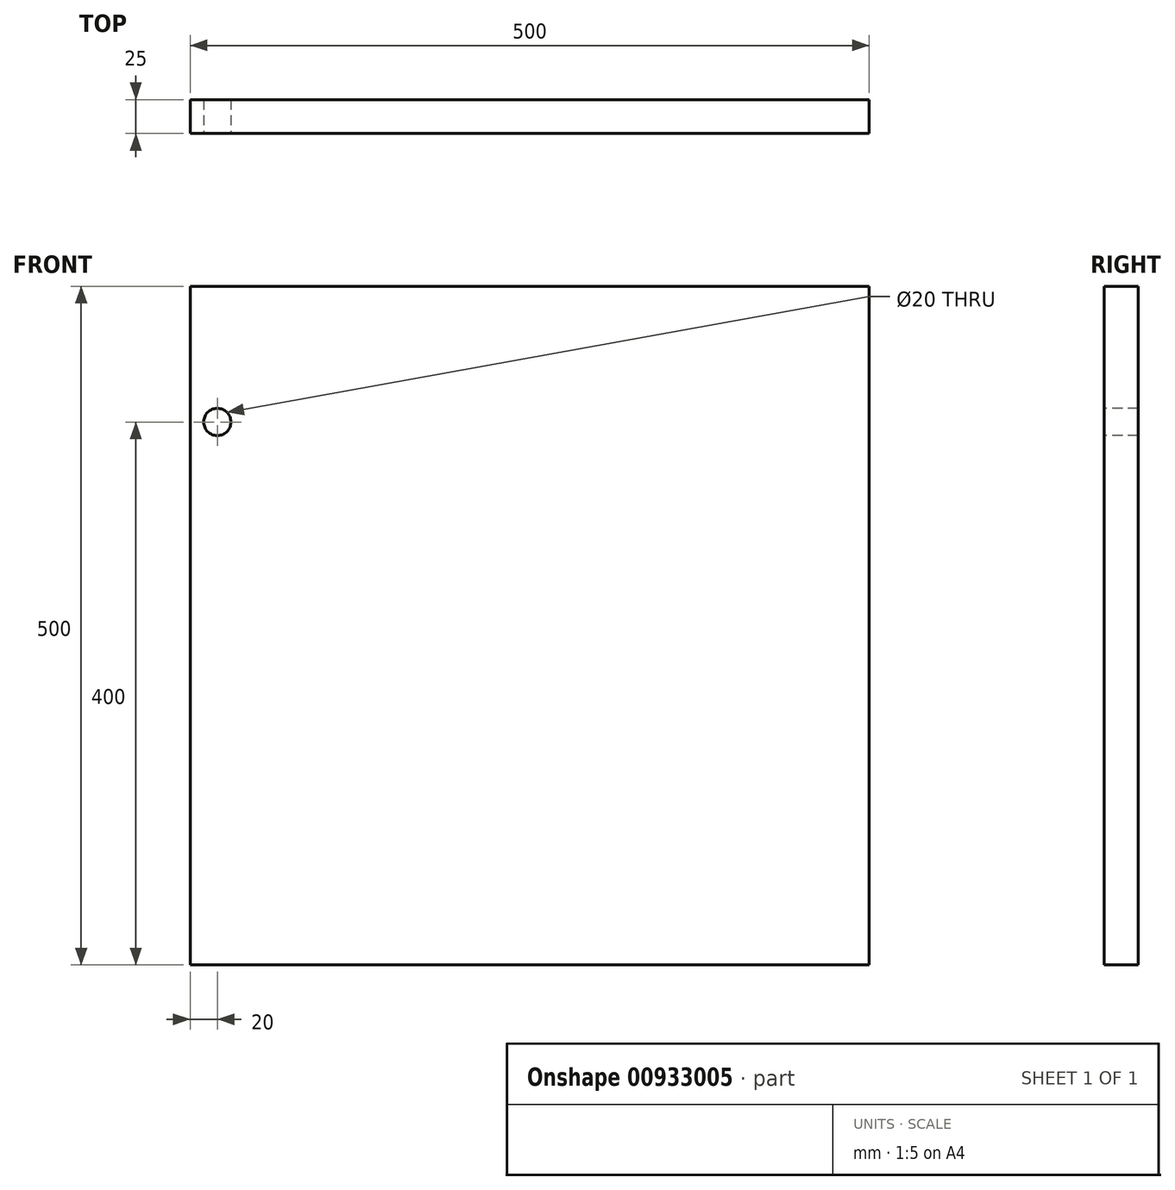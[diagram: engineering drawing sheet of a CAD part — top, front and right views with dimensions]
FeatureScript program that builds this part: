
annotation { "Feature Type Name" : "Feature", "Feature Type Description" : "" }
export const myFeature = defineFeature(function(context is Context, id is Id, definition is map)
    precondition{}
    {
        {
            var Q0;
            Q0=qCreatedBy(makeId("Front.planeOp"),FACE);
            var sketch = newSketch(context, id + "F0", { "sketchPlane" : qUnion([Q0])});
            skLineSegment(sketch, "E0.bottom", {"start": v(0, 0) * mm, "end": v(500, 0) * mm});
            skLineSegment(sketch, "E0.top", {"start": v(0, -500) * mm, "end": v(500, -500) * mm});
            skLineSegment(sketch, "E0.left", {"start": v(0, 0) * mm, "end": v(0, -500) * mm});
            skLineSegment(sketch, "E0.right", {"start": v(500, 0) * mm, "end": v(500, -500) * mm});
            skSolve(sketch);
        }
        {
            var Q0;
            Q0 = qSketchRegion(id + "F0", true);
            extrude(context, id + "F1", {"entities" : qUnion([Q0]), "depth" : 25 * mm, "offsetDistance" : 25 * mm});
        }
        {
            var Q0;
            Q0=makeQuery(id+"F1.opExtrude","CAP_FACE",FACE,{"disambiguationData":[OSD([sQuery(id+"F0.wireOp",EDGE,"E0.bottom"),sQuery(id+"F0.wireOp",EDGE,"E0.top"),sQuery(id+"F0.wireOp",EDGE,"E0.left"),sQuery(id+"F0.wireOp",EDGE,"E0.right")])],"isStart":false});
            var sketch = newSketch(context, id + "F2", { "sketchPlane" : qUnion([Q0])});
            skLineSegment(sketch, "E1", {"start": v(0, -500) * mm, "end": v(20, -500) * mm});
            skLineSegment(sketch, "E2", {"start": v(20, -500) * mm, "end": v(20, -100) * mm});
            skCircle(sketch, "E3", {"center": v(20, -100) * mm, "radius": 10 * mm});
            skSolve(sketch);
        }
        {
            var Q0;
            Q0 = qSketchRegion(id + "F2", true);
            extrude(context, id + "F3", {"entities" : qUnion([Q0]), "operationType" : NewBodyOperationType.REMOVE, "oppositeDirection" : true, "depth" : 25 * mm, "offsetDistance" : 25 * mm});
        }
    });
